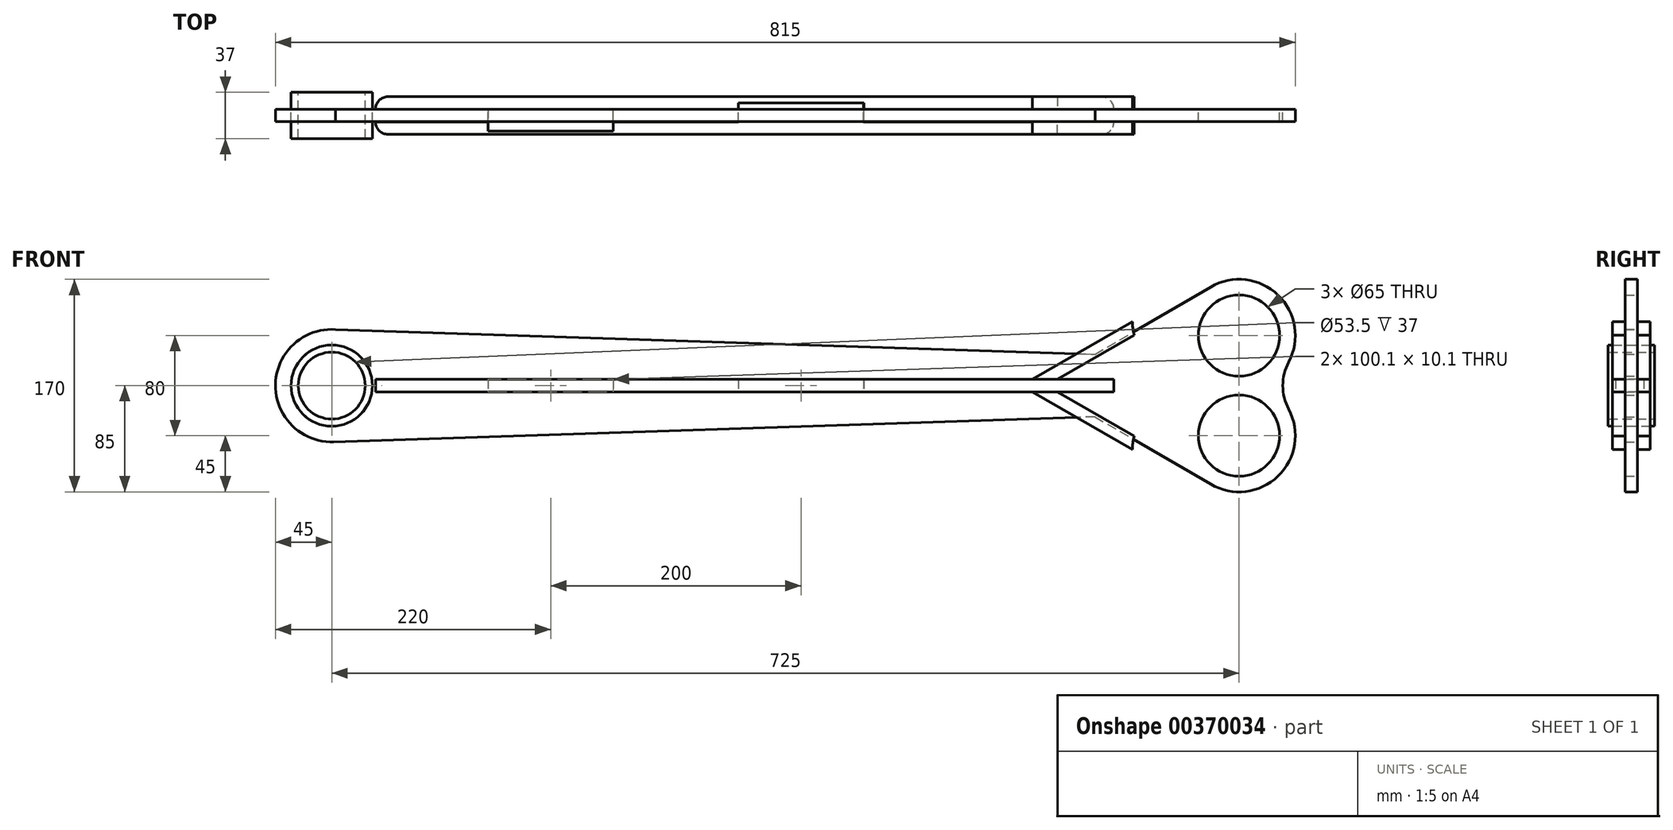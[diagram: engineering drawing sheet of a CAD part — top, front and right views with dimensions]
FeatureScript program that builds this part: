
annotation { "Feature Type Name" : "Feature", "Feature Type Description" : "" }
export const myFeature = defineFeature(function(context is Context, id is Id, definition is map)
    precondition{}
    {
        {
            var Q0;
            Q0=qCreatedBy(makeId("Front.planeOp"),FACE);
            var sketch = newSketch(context, id + "F0", { "sketchPlane" : qUnion([Q0])});
            skCircle(sketch, "E0", {"center": v(0, 0) * mm, "radius": 32.5 * mm});
            skCircle(sketch, "E1", {"center": v(0, 0) * mm, "radius": 45 * mm});
            skCircle(sketch, "E2", {"center": v(850, 0) * mm, "radius": 32.5 * mm, "construction": true});
            skCircle(sketch, "E3", {"center": v(725, 40) * mm, "radius": 32.5 * mm});
            skCircle(sketch, "E4", {"center": v(725, -40) * mm, "radius": 32.5 * mm});
            skCircle(sketch, "E5", {"center": v(725, 40) * mm, "radius": 45 * mm});
            skArc(sketch, "E6", {"start": v(702.32, -78.87) * mm, "mid": v(756.2, -72.42) * mm, "end": v(764.7, -18.82) * mm});
            skLineSegment(sketch, "E7", {"start": v(610, 25) * mm, "end": v(610, -25) * mm, "construction": true});
            skPoint(sketch, "E8", {"position": v(610, 0) * mm});
            skLineSegment(sketch, "E9", {"start": v(0, 45) * mm, "end": v(610, 25) * mm});
            skLineSegment(sketch, "E10", {"start": v(610, -25) * mm, "end": v(0, -45.02) * mm});
            skLineSegment(sketch, "E11", {"start": v(610, 25) * mm, "end": v(702.32, 78.87) * mm});
            skLineSegment(sketch, "E12", {"start": v(610, -25) * mm, "end": v(702.32, -78.87) * mm});
            skArc(sketch, "E13", {"start": v(764.7, 18.82) * mm, "mid": v(760, 0) * mm, "end": v(764.7, -18.82) * mm});
            skLineSegment(sketch, "E14.bottom", {"start": v(124.95, 5.05) * mm, "end": v(225.05, 5.05) * mm});
            skLineSegment(sketch, "E14.top", {"start": v(124.95, -5.05) * mm, "end": v(225.05, -5.05) * mm});
            skLineSegment(sketch, "E14.left", {"start": v(124.95, 5.05) * mm, "end": v(124.95, -5.05) * mm});
            skLineSegment(sketch, "E14.right", {"start": v(225.05, 5.05) * mm, "end": v(225.05, -5.05) * mm});
            skLineSegment(sketch, "E15.bottom", {"start": v(324.95, 5.05) * mm, "end": v(425.05, 5.05) * mm});
            skLineSegment(sketch, "E15.top", {"start": v(324.95, -5.05) * mm, "end": v(425.05, -5.05) * mm});
            skLineSegment(sketch, "E15.left", {"start": v(324.95, 5.05) * mm, "end": v(324.95, -5.05) * mm});
            skLineSegment(sketch, "E15.right", {"start": v(425.05, 5.05) * mm, "end": v(425.05, -5.05) * mm});
            skSolve(sketch);
        }
        {
            var Q0;
            Q0=qSketchRegion(id+"F0",true);
            extrude(context, id + "F1", {"entities" : qUnion([Q0]), "depth" : 5 * mm, "hasSecondDirection" : true, "secondDirectionOppositeDirection" : true, "secondDirectionDepth" : 5 * mm});
        }
        {
            var Q0;
            Q0=qCreatedBy(makeId("Top.planeOp"),FACE);
            var sketch = newSketch(context, id + "F2", { "sketchPlane" : qUnion([Q0])});
            skLineSegment(sketch, "E16", {"start": v(35, 5.05) * mm, "end": v(35, 5.05) * mm});
            skLineSegment(sketch, "E17", {"start": v(45, 15.05) * mm, "end": v(615, 15.05) * mm});
            skLineSegment(sketch, "E18", {"start": v(35, 5.05) * mm, "end": v(324.9, 5.05) * mm});
            skLineSegment(sketch, "E19", {"start": v(625, 5.05) * mm, "end": v(625, 5.05) * mm});
            skLineSegment(sketch, "E20", {"start": v(125, 5.05) * mm, "end": v(125, -12.45) * mm});
            skLineSegment(sketch, "E21", {"start": v(125, -12.45) * mm, "end": v(225, -12.45) * mm});
            skLineSegment(sketch, "E22", {"start": v(225, -12.45) * mm, "end": v(225, 5.05) * mm});
            skLineSegment(sketch, "E23", {"start": v(324.9, 5.05) * mm, "end": v(324.9, 10.15) * mm});
            skLineSegment(sketch, "E24", {"start": v(324.9, 10.15) * mm, "end": v(425.1, 10.15) * mm});
            skLineSegment(sketch, "E25", {"start": v(425.1, 10.15) * mm, "end": v(425.1, 5.05) * mm});
            skLineSegment(sketch, "E26.trimOffspring", {"start": v(425.1, 5.05) * mm, "end": v(625, 5.05) * mm});
            skPoint(sketch, "E27.visualSharp", {"position": v(35, 15.05) * mm});
            skArc(sketch, "E27.filletArc", {"start": v(45, 15.05) * mm, "mid": v(37.93, 12.12) * mm, "end": v(35, 5.05) * mm});
            skPoint(sketch, "E28.visualSharp", {"position": v(625, 15.05) * mm});
            skArc(sketch, "E28.filletArc", {"start": v(625, 5.05) * mm, "mid": v(622.07, 12.12) * mm, "end": v(615, 15.05) * mm});
            skLineSegment(sketch, "E29", {"start": v(35, -5.05) * mm, "end": v(35, -5.05) * mm});
            skLineSegment(sketch, "E30", {"start": v(45, -15.05) * mm, "end": v(615, -15.05) * mm});
            skLineSegment(sketch, "E31", {"start": v(625, -5.05) * mm, "end": v(625, -5.05) * mm});
            skLineSegment(sketch, "E32", {"start": v(625, -5.05) * mm, "end": v(225.05, -5.05) * mm});
            skLineSegment(sketch, "E33", {"start": v(124.95, -5.05) * mm, "end": v(124.95, -12.55) * mm});
            skLineSegment(sketch, "E34", {"start": v(124.95, -12.55) * mm, "end": v(225.05, -12.55) * mm});
            skLineSegment(sketch, "E35", {"start": v(225.05, -12.55) * mm, "end": v(225.05, -5.05) * mm});
            skLineSegment(sketch, "E36.trimOffspring", {"start": v(124.95, -5.05) * mm, "end": v(35, -5.05) * mm});
            skLineSegment(sketch, "E37", {"start": v(325, -5.05) * mm, "end": v(325, 10.05) * mm});
            skLineSegment(sketch, "E38", {"start": v(325, 10.05) * mm, "end": v(425, 10.05) * mm});
            skLineSegment(sketch, "E39", {"start": v(425, 10.05) * mm, "end": v(425, -5.05) * mm});
            skPoint(sketch, "E40.visualSharp", {"position": v(625, -15.05) * mm});
            skArc(sketch, "E40.filletArc", {"start": v(615, -15.05) * mm, "mid": v(622.07, -12.12) * mm, "end": v(625, -5.05) * mm});
            skPoint(sketch, "E41.visualSharp", {"position": v(35, -15.05) * mm});
            skArc(sketch, "E41.filletArc", {"start": v(35, -5.05) * mm, "mid": v(37.93, -12.12) * mm, "end": v(45, -15.05) * mm});
            skSolve(sketch);
        }
        {
            var Q0;
            Q0=qSketchRegion(id+"F2",true);
            extrude(context, id + "F3", {"entities" : qUnion([Q0]), "depth" : 5 * mm, "hasSecondDirection" : true, "secondDirectionOppositeDirection" : true, "secondDirectionDepth" : 5 * mm});
        }
        {
            var Q0;
            Q0=makeQuery(id+"F1.opExtrude","CAP_FACE",FACE,{"disambiguationData":[OSD([sQuery(id+"F0.wireOp",EDGE,"E0"),sQuery(id+"F0.wireOp",EDGE,"E1"),sQuery(id+"F0.wireOp",EDGE,"E3"),sQuery(id+"F0.wireOp",EDGE,"E4"),sQuery(id+"F0.wireOp",EDGE,"E5"),sQuery(id+"F0.wireOp",EDGE,"E6"),sQuery(id+"F0.wireOp",EDGE,"E9"),sQuery(id+"F0.wireOp",EDGE,"E10"),sQuery(id+"F0.wireOp",EDGE,"E11"),sQuery(id+"F0.wireOp",EDGE,"E12"),sQuery(id+"F0.wireOp",EDGE,"E13"),sQuery(id+"F0.wireOp",EDGE,"E14.bottom"),sQuery(id+"F0.wireOp",EDGE,"E14.top"),sQuery(id+"F0.wireOp",EDGE,"E14.left"),sQuery(id+"F0.wireOp",EDGE,"E14.right"),sQuery(id+"F0.wireOp",EDGE,"E15.bottom"),sQuery(id+"F0.wireOp",EDGE,"E15.top"),sQuery(id+"F0.wireOp",EDGE,"E15.left"),sQuery(id+"F0.wireOp",EDGE,"E15.right")])],"isStart":true});
            var sketch = newSketch(context, id + "F4", { "sketchPlane" : qUnion([Q0])});
            skLineSegment(sketch, "E42", {"start": v(-641.22, -40.45) * mm, "end": v(-580, -5.1) * mm});
            skLineSegment(sketch, "E43", {"start": v(-580, -5.1) * mm, "end": v(-560, -5.1) * mm});
            skLineSegment(sketch, "E44", {"start": v(-560, -5.1) * mm, "end": v(-639.92, -51.24) * mm});
            skCircle(sketch, "E45", {"center": v(-675, -50) * mm, "radius": 35.1 * mm, "construction": true});
            skArc(sketch, "E46", {"start": v(-639.92, -51.24) * mm, "mid": v(-640.15, -45.8) * mm, "end": v(-641.22, -40.45) * mm});
            skLineSegment(sketch, "E47.MirrorCS", {"start": v(-580, 5.1) * mm, "end": v(-560, 5.1) * mm});
            skArc(sketch, "E48.MirrorCS", {"start": v(-639.92, 51.24) * mm, "mid": v(-640.15, 45.8) * mm, "end": v(-641.22, 40.45) * mm});
            skLineSegment(sketch, "E49.MirrorCS", {"start": v(-641.22, 40.45) * mm, "end": v(-580, 5.1) * mm});
            skLineSegment(sketch, "E50.MirrorCS", {"start": v(-560, 5.1) * mm, "end": v(-639.92, 51.24) * mm});
            skSolve(sketch);
        }
        {
            var Q0;
            Q0=qSketchRegion(id+"F4",true);
            extrude(context, id + "F5", {"entities" : qUnion([Q0]), "depth" : 10 * mm});
        }
        {
            var Q0;
            Q0=makeQuery(id+"F5.opExtrude","SWEPT_BODY",BODY,{"disambiguationData":[OSD([sQuery(id+"F4.wireOp",EDGE,"E47.MirrorCS"),sQuery(id+"F4.wireOp",EDGE,"E48.MirrorCS"),sQuery(id+"F4.wireOp",EDGE,"E49.MirrorCS"),sQuery(id+"F4.wireOp",EDGE,"E50.MirrorCS")])]});
            var Q1;
            Q1=makeQuery(id+"F5.opExtrude","SWEPT_BODY",BODY,{"disambiguationData":[OSD([sQuery(id+"F4.wireOp",EDGE,"E42"),sQuery(id+"F4.wireOp",EDGE,"E43"),sQuery(id+"F4.wireOp",EDGE,"E44"),sQuery(id+"F4.wireOp",EDGE,"E46")])]});
            var Q2;
            Q2=qCreatedBy(makeId("Front.planeOp"),FACE);
            mirror(context, id + "F6", {"entities" : qUnion([Q0, Q1]), "mirrorPlane" : qUnion([Q2])});
        }
        {
            var Q0;
            Q0=qCreatedBy(makeId("Front.planeOp"),FACE);
            var sketch = newSketch(context, id + "F7", { "sketchPlane" : qUnion([Q0])});
            skCircle(sketch, "E51", {"center": v(0, 0) * mm, "radius": 32.45 * mm});
            skCircle(sketch, "E52", {"center": v(0, 0) * mm, "radius": 26.75 * mm});
            skSolve(sketch);
        }
        {
            var Q0;
            Q0=qSketchRegion(id+"F7",true);
            extrude(context, id + "F8", {"entities" : qUnion([Q0]), "depth" : 18.5 * mm, "hasSecondDirection" : true, "secondDirectionOppositeDirection" : true, "secondDirectionDepth" : 18.5 * mm});
        }
    });
